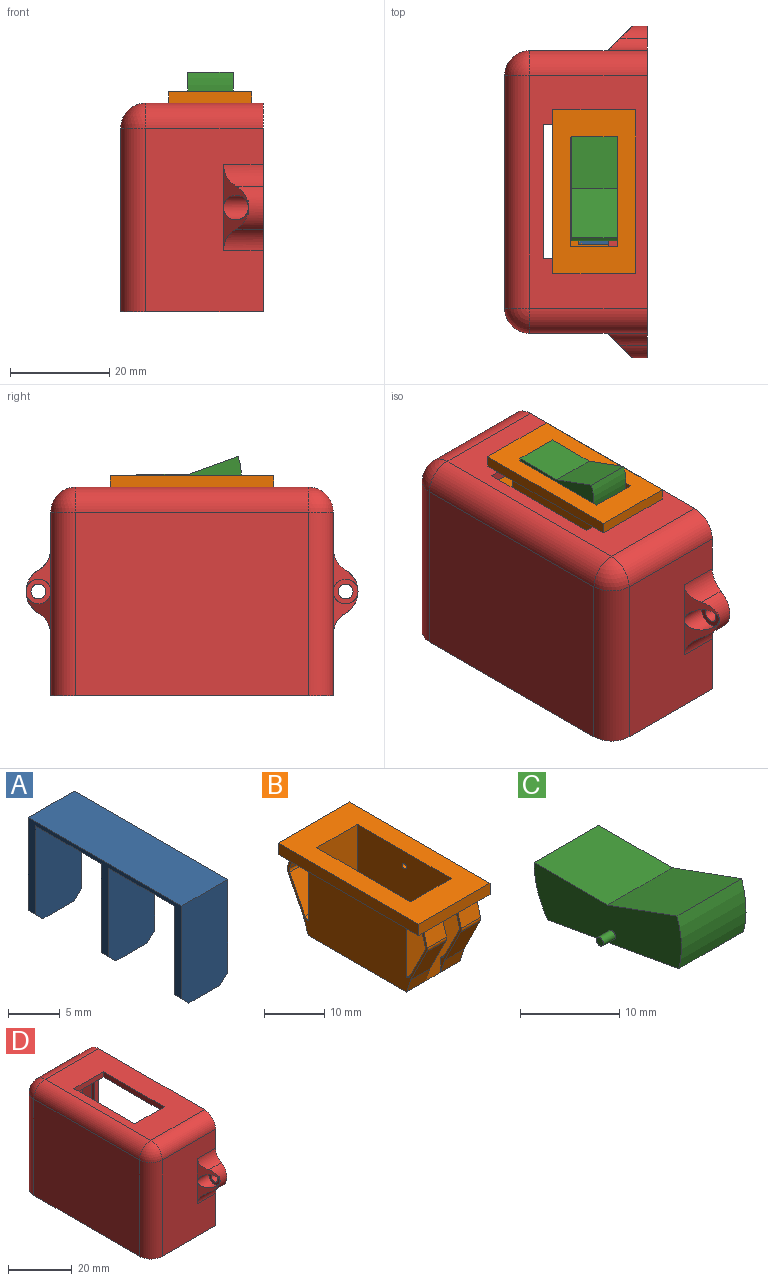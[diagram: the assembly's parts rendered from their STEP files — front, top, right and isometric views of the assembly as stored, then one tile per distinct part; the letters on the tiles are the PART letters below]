
ASSEMBLY  parts=4 mates=3
PART A: 20 faces, bbox 6.3x21x12 mm
  f0: plane 9x6.3mm, normal (0,0,-1), area 56.7mm2, adj f2,f4,f10,f12
  f1: plane 9x6.3mm, normal (0,0,-1), area 56.7mm2, adj f2,f4,f7,f9
  f2: plane 21x11mm, normal (-1,0,0), area 42mm2, adj f0,f1,f3,f5,f6,f7,f9,f10
  f3: plane 12x6.3mm, normal (0,-1,0), area 74.6mm2, adj f2,f4,f6,f13,f14,f15
  f4: plane 21x11mm, normal (1,0,0), area 42mm2, adj f0,f1,f3,f5,f6,f7,f9,f10
  f5: plane 12x6.3mm, normal (0,1,0), area 74.6mm2, adj f2,f4,f6,f8,f18,f19
  f6: plane 21x6.3mm, normal (0,0,1), area 132.3mm2, adj f2,f3,f4,f5
  f7: plane 11.5x6.3mm, normal (0,-1,0), area 71.5mm2, adj f1,f2,f4,f8,f18,f19
  f8: plane 4.3x1mm, normal (0,0,-1), area 4.3mm2, adj f5,f7,f18,f19
  f9: plane 11.5x6.3mm, normal (0,1,0), area 71.5mm2, adj f1,f2,f4,f11,f16,f17
  f10: plane 11.5x6.3mm, normal (0,-1,0), area 71.5mm2, adj f0,f2,f4,f11,f16,f17
  f11: plane 4.3x1mm, normal (0,0,-1), area 4.3mm2, adj f9,f10,f16,f17
  f12: plane 11.5x6.3mm, normal (0,1,0), area 71.5mm2, adj f0,f2,f4,f13,f14,f15
  f13: plane 4.3x1mm, normal (0,0,-1), area 4.3mm2, adj f3,f12,f14,f15
  f14: plane 1x1mm, normal (-0.71,0,-0.71), area 1.4mm2, adj f2,f3,f12,f13
  f15: plane 1x1mm, normal (0.71,0,-0.71), area 1.4mm2, adj f3,f4,f12,f13
  f16: plane 1x1mm, normal (-0.71,0,-0.71), area 1.4mm2, adj f2,f9,f10,f11
  f17: plane 1x1mm, normal (0.71,0,-0.71), area 1.4mm2, adj f4,f9,f10,f11
  f18: plane 1x1mm, normal (0.71,0,-0.71), area 1.4mm2, adj f4,f5,f7,f8
  f19: plane 1x1mm, normal (-0.71,0,-0.71), area 1.4mm2, adj f2,f5,f7,f8
PART B: 62 faces, bbox 16.7x33x17.3 mm
  f0: plane 7.11x4.5mm, normal (0,-0.89,0.45), area 35.8mm2, adj f13,f43,f52,f58
  f1: plane 4.5x2.93mm, normal (0,0.95,-0.32), area 13.9mm2, adj f13,f14,f43,f57
  f2: plane 4.5x3.13mm, normal (0,-0.96,-0.27), area 14.6mm2, adj f5,f13,f43,f52
  f3: plane 7.59x4.5mm, normal (0,0.89,-0.45), area 38.2mm2, adj f13,f43,f53,f57
  f4: plane 4.5x3.13mm, normal (0,0.96,0.27), area 14.6mm2, adj f5,f13,f43,f53
  f5: plane 4.5x0.5mm, normal (0,0,1), area 2.3mm2, adj f2,f4,f13,f43
  f6: plane 4.5x2.93mm, normal (0,-0.95,-0.32), area 13.9mm2, adj f12,f14,f41,f50
  f7: plane 7.11x4.5mm, normal (0,0.89,0.45), area 35.8mm2, adj f12,f41,f48,f49
  f8: plane 4.5x3.13mm, normal (0,0.96,-0.27), area 14.6mm2, adj f10,f12,f41,f49
  f9: plane 7.59x4.5mm, normal (0,-0.89,-0.45), area 38.2mm2, adj f12,f41,f50,f51
  f10: plane 4.5x0.5mm, normal (0,0,1), area 2.3mm2, adj f8,f11,f12,f41
  f11: plane 4.5x3.13mm, normal (0,-0.96,0.27), area 14.6mm2, adj f10,f12,f41,f51
  f12: plane 32.86x15mm, normal (1,0,0), area 358.8mm2, adj f6,f7,f8,f9,f10,f11,f14,f20
  f13: plane 32.86x15mm, normal (-1,0,0), area 358.8mm2, adj f0,f1,f2,f3,f4,f5,f14,f20
  f14: plane 23x12.5mm, normal (0,0,-1), area 287.5mm2, adj f1,f6,f12,f13,f26,f27,f29,f30
  f15: plane 33x16.7mm, normal (0,0,1), area 342.1mm2, adj f16,f17,f18,f19,f21,f22,f23,f24
  f16: plane 33x2.3mm, normal (1,0,0), area 75.9mm2, adj f15,f17,f19,f20
  f17: plane 16.7x2.3mm, normal (0,1,0), area 38.4mm2, adj f15,f16,f18,f20
  f18: plane 33x2.3mm, normal (-1,0,0), area 75.9mm2, adj f15,f17,f19,f20
  f19: plane 16.7x2.3mm, normal (0,-1,0), area 38.4mm2, adj f15,f16,f18,f20
  f20: plane 33x16.7mm, normal (0,0,-1), area 263.6mm2, adj f12,f13,f16,f17,f18,f19,f27,f29
  f21: plane 22x14.8mm, normal (-1,0,0), area 324.8mm2, adj f15,f22,f24,f25,f61
  f22: plane 14.8x9.5mm, normal (0,-1,0), area 140.6mm2, adj f15,f21,f23,f25
  f23: plane 22x14.8mm, normal (1,0,0), area 324.8mm2, adj f15,f22,f24,f25,f60
  f24: plane 14.8x9.5mm, normal (0,1,0), area 140.6mm2, adj f15,f21,f23,f25
  f25: plane 22x9.5mm, normal (0,0,1), area 209mm2, adj f21,f22,f23,f24
  f26: plane 4.5x2.93mm, normal (0,-0.95,-0.32), area 13.9mm2, adj f13,f14,f40,f59
  f27: plane 15x12.5mm, normal (0,-1,0), area 160.5mm2, adj f12,f13,f14,f20,f40,f41,f48,f54
  f28: plane 7.11x4.5mm, normal (0,-0.89,0.45), area 35.8mm2, adj f12,f42,f44,f45
  f29: plane 15x12.5mm, normal (0,1,0), area 160.5mm2, adj f12,f13,f14,f20,f42,f43,f44,f58
  f30: plane 4.5x2.93mm, normal (0,0.95,-0.32), area 13.9mm2, adj f12,f14,f42,f46
  f31: plane 7.11x4.5mm, normal (0,0.89,0.45), area 35.8mm2, adj f13,f40,f54,f55
  f32: plane 4.5x3.13mm, normal (0,0.96,-0.27), area 14.6mm2, adj f13,f34,f40,f55
  f33: plane 7.59x4.5mm, normal (0,-0.89,-0.45), area 38.2mm2, adj f13,f40,f56,f59
  f34: plane 4.5x0.5mm, normal (0,0,1), area 2.3mm2, adj f13,f32,f35,f40
  f35: plane 4.5x3.13mm, normal (0,-0.96,0.27), area 14.6mm2, adj f13,f34,f40,f56
  f36: plane 4.5x3.13mm, normal (0,-0.96,-0.27), area 14.6mm2, adj f12,f39,f42,f45
  f37: plane 7.59x4.5mm, normal (0,0.89,-0.45), area 38.2mm2, adj f12,f42,f46,f47
  f38: plane 4.5x3.13mm, normal (0,0.96,0.27), area 14.6mm2, adj f12,f39,f42,f47
  f39: plane 4.5x0.5mm, normal (0,0,1), area 2.3mm2, adj f12,f36,f38,f42
  f40: plane 14.5x4.93mm, normal (1,0,0), area 7.3mm2, adj f26,f27,f31,f32,f33,f34,f35,f54
  f41: plane 14.5x4.93mm, normal (-1,0,0), area 7.3mm2, adj f6,f7,f8,f9,f10,f11,f27,f48
  f42: plane 14.5x4.93mm, normal (-1,0,0), area 7.3mm2, adj f28,f29,f30,f36,f37,f38,f39,f44
  f43: plane 14.5x4.93mm, normal (1,0,0), area 7.3mm2, adj f0,f1,f2,f3,f4,f5,f29,f52
  f44: cylinder r=1mm len=4.5mm, axis (-1,0,0), area 4.4mm2, adj f12,f28,f29,f42
  f45: cylinder r=1mm len=4.5mm, axis (-1,0,0), area 3.3mm2, adj f12,f28,f36,f42
  f46: cylinder r=1mm len=4.5mm, axis (1,0,0), area 0.6mm2, adj f12,f30,f37,f42
  f47: cylinder r=1mm len=4.5mm, axis (1,0,0), area 3.3mm2, adj f12,f37,f38,f42
  f48: cylinder r=1mm len=4.5mm, axis (1,0,0), area 4.4mm2, adj f7,f12,f27,f41
  f49: cylinder r=1mm len=4.5mm, axis (-1,0,0), area 3.3mm2, adj f7,f8,f12,f41
  f50: cylinder r=1mm len=4.5mm, axis (1,0,0), area 0.6mm2, adj f6,f9,f12,f41
  f51: cylinder r=1mm len=4.5mm, axis (1,0,0), area 3.3mm2, adj f9,f11,f12,f41
  f52: cylinder r=1mm len=4.5mm, axis (-1,0,0), area 3.3mm2, adj f0,f2,f13,f43
  f53: cylinder r=1mm len=4.5mm, axis (1,0,0), area 3.3mm2, adj f3,f4,f13,f43
  f54: cylinder r=1mm len=4.5mm, axis (1,0,0), area 4.4mm2, adj f13,f27,f31,f40
  f55: cylinder r=1mm len=4.5mm, axis (-1,0,0), area 3.3mm2, adj f13,f31,f32,f40
  f56: cylinder r=1mm len=4.5mm, axis (1,0,0), area 3.3mm2, adj f13,f33,f35,f40
  f57: cylinder r=1mm len=4.5mm, axis (1,0,0), area 0.6mm2, adj f1,f3,f13,f43
  f58: cylinder r=1mm len=4.5mm, axis (-1,0,0), area 4.4mm2, adj f0,f13,f29,f43
  f59: cylinder r=1mm len=4.5mm, axis (1,0,0), area 0.6mm2, adj f13,f26,f33,f40
  f60: cylinder r=0.5mm len=1.5mm, axis (1,0,0), area 4.7mm2, adj f13,f23
  f61: cylinder r=0.5mm len=1.5mm, axis (1,0,0), area 4.7mm2, adj f12,f21
PART C: 11 faces, bbox 12.6x21x9.7 mm
  f0: cylinder r=10.5mm len=9.2mm, axis (-1,0,0), area 59.6mm2, adj f1,f4,f5,f6
  f1: plane 18.69x9.2mm, normal (0,-0.17,-0.98), area 174.6mm2, adj f0,f2,f5,f6
  f2: cylinder r=10.5mm len=9.2mm, axis (-1,0,0), area 59.6mm2, adj f1,f3,f5,f6
  f3: plane 10.5x9.2mm, normal (0,0,1), area 96.6mm2, adj f2,f4,f5,f6
  f4: plane 9.87x9.2mm, normal (0,0.34,0.94), area 96.6mm2, adj f0,f3,f5,f6
  f5: plane 21x9.67mm, normal (1,0,0), area 110mm2, adj f0,f1,f2,f3,f4,f9
  f6: plane 21x9.67mm, normal (-1,0,0), area 110mm2, adj f0,f1,f2,f3,f4,f8
  f7: plane 1x1mm, normal (-1,0,0), area 0.8mm2, adj f8
  f8: cylinder r=0.5mm len=1.72mm, axis (-1,0,0), area 5.4mm2, adj f6,f7
  f9: cylinder r=0.5mm len=1.72mm, axis (-1,0,0), area 5.4mm2, adj f5,f10
  f10: plane 1x1mm, normal (1,0,0), area 0.8mm2, adj f9
PART D: 47 faces, bbox 28.7x66.9x42 mm
  f0: plane 56.85x28.69mm, normal (0,0,-1), area 229.7mm2, adj f5,f6,f7,f8,f15,f16,f17,f18
  f1: cylinder r=1.5mm len=3mm, axis (1,0,0), area 28.3mm2, adj f7,f28
  f2: cylinder r=1.5mm len=3mm, axis (1,0,0), area 28.3mm2, adj f7,f30
  f3: plane 8.66x5mm, normal (-0.71,0.71,0), area 16.7mm2, adj f8,f20,f22,f29
  f4: plane 8.66x5mm, normal (-0.71,-0.71,0), area 16.7mm2, adj f5,f19,f24,f27
  f5: plane 37x23.69mm, normal (0,-1,0), area 737.9mm2, adj f0,f4,f7,f23,f24,f26,f44,f46
  f6: plane 46.85x37mm, normal (-1,0,0), area 1733.5mm2, adj f0,f40,f43,f46
  f7: plane 66.85x42mm, normal (1,0,0), area 716mm2, adj f0,f1,f2,f5,f8,f9,f19,f20
  f8: plane 37x23.69mm, normal (0,1,0), area 737.9mm2, adj f0,f3,f7,f21,f22,f25,f40,f41
  f9: plane 46.85x23.69mm, normal (0,0,1), area 758.9mm2, adj f7,f11,f12,f13,f14,f41,f43,f44
  f10: plane 52.85x20.69mm, normal (0,0,-1), area 742.4mm2, adj f11,f12,f13,f14,f16,f18,f35,f38
  f11: plane 13x2mm, normal (0,-1,0), area 26mm2, adj f9,f10,f12,f14
  f12: plane 27x2mm, normal (1,0,0), area 54mm2, adj f9,f10,f11,f13
  f13: plane 13x2mm, normal (0,1,0), area 26mm2, adj f9,f10,f12,f14
  f14: plane 27x2mm, normal (-1,0,0), area 54mm2, adj f9,f10,f11,f13
  f15: plane 48.85x38mm, normal (1,0,0), area 1856.4mm2, adj f0,f34,f35,f36
  f16: plane 40x20.69mm, normal (0,1,0), area 827.5mm2, adj f0,f10,f36,f37
  f17: plane 48.85x38mm, normal (-1,0,0), area 122.9mm2, adj f0,f31,f32,f33,f37,f38,f39
  f18: plane 40x20.69mm, normal (0,-1,0), area 827.5mm2, adj f0,f10,f34,f39
  f19: cylinder r=5mm len=8.66mm, axis (1,0,0), area 40.5mm2, adj f4,f7,f23,f24,f26
  f20: cylinder r=5mm len=8.66mm, axis (1,0,0), area 40.5mm2, adj f3,f7,f21,f22,f25
  f21: cylinder r=5mm len=8mm, axis (1,0,0), area 37.4mm2, adj f7,f8,f20,f25
  f22: cylinder r=5mm len=8mm, axis (1,0,0), area 37.4mm2, adj f3,f7,f8,f20
  f23: cylinder r=5mm len=8mm, axis (1,0,0), area 37.4mm2, adj f5,f7,f19,f26
  f24: cylinder r=5mm len=8mm, axis (1,0,0), area 37.4mm2, adj f4,f5,f7,f19
  f25: plane 8.66x5mm, normal (-0.71,0.71,0), area 16.7mm2, adj f8,f20,f21,f29
  f26: plane 8.66x5mm, normal (-0.71,-0.71,0), area 16.7mm2, adj f5,f19,f23,f27
  f27: cylinder r=2.5mm len=5mm, axis (-1,0,0), area 39.3mm2, adj f4,f26,f28
  f28: plane 5x5mm, normal (-1,0,0), area 12.6mm2, adj f1,f27
  f29: cylinder r=2.5mm len=5mm, axis (-1,0,0), area 39.3mm2, adj f3,f25,f30
  f30: plane 5x5mm, normal (-1,0,0), area 12.6mm2, adj f2,f29
  f31: plane 37x2mm, normal (0,-1,0), area 74mm2, adj f0,f7,f17,f33
  f32: plane 37x2mm, normal (0,1,0), area 74mm2, adj f0,f7,f17,f33
  f33: plane 46.85x2mm, normal (0,0,-1), area 93.7mm2, adj f7,f17,f31,f32
  f34: plane 40x2mm, normal (0.71,-0.71,0), area 110.3mm2, adj f0,f15,f18,f35
  f35: plane 52.85x2mm, normal (0.71,0,-0.71), area 143.8mm2, adj f10,f15,f34,f36
  f36: plane 40x2mm, normal (0.71,0.71,0), area 110.3mm2, adj f0,f15,f16,f35
  f37: plane 40x2mm, normal (-0.71,0.71,0), area 110.3mm2, adj f0,f16,f17,f38
  f38: plane 52.85x2mm, normal (-0.71,0,-0.71), area 143.8mm2, adj f10,f17,f37,f39
  f39: plane 40x2mm, normal (-0.71,-0.71,0), area 110.3mm2, adj f0,f17,f18,f38
  f40: cylinder r=5mm len=37mm, axis (0,0,-1), area 290.6mm2, adj f0,f6,f8,f42
  f41: cylinder r=5mm len=23.69mm, axis (1,0,0), area 186mm2, adj f7,f8,f9,f42
  f42: sphere r=5mm, area 39.3mm2, adj f40,f41,f43
  f43: cylinder r=5mm len=46.85mm, axis (0,1,0), area 368mm2, adj f6,f9,f42,f45
  f44: cylinder r=5mm len=23.69mm, axis (-1,0,0), area 186mm2, adj f5,f7,f9,f45
  f45: sphere r=5mm, area 39.3mm2, adj f43,f44,f46
  f46: cylinder r=5mm len=37mm, axis (0,0,1), area 290.6mm2, adj f0,f5,f6,f45
PLACE A t=(0.1,-0.18,5.03)mm
PLACE B t=(0.1,-0.18,5.03)mm
PLACE C t=(0.14,-0.18,5.03)mm
PLACE D t=(-3.56,-0.18,18.03)mm
MATE fastened A.f6 <-> B.f25  axis (0,0,1) through (0.1,-0.18,7.53)mm
MATE fastened D.f9 <-> B.f20  axis (0,0,1) through (0.1,-0.18,20.03)mm
MATE revolute B.f60 <-> C.f8  axis (1,0,0) through (5.6,-0.18,19.34)mm
